# Revit family: Ebara-Grupo de presión APG VV (350-ES-600)
name_source: partatom
category: Equipos mecánicos
revit_build: Autodesk Revit 2017 (Build: 20171027_0315(x64)
units: mm (PartAtom-declared; Revit-internal decimal feet)

## family parameters
Compartido = No
Corte con vacíos al cargar = No
Cota de conector redondo = Diámetro de uso
Número OmniClass = 23.65.05.11.11
Punto de cálculo de habitación = No
Se basa en plano de trabajo = No
Siempre vertical = Sí
Tipo de pieza = Normal
Título OmniClass = Water Supply Systems

## types (1)
- Ebara-Grupo de presión APG VV (350-ES-600)
    Acabado armario = 09 96_Genérico_Esmalte blanco 255.255.255
    Acabado coloreado = 09 96_Genérico_Esmalte azul 30.137.225
    Acabado conexiones tuberías = 22 11_Genérico_Latón pulido
    Acabado estructura = 09 96_Genérico_Esmalte negro 22.22.22
    Acabado plástico gris = 06 60_Genérico_Plástico gris mate 128.128.128
    Acabado tuberías = 05 12_Genérico_Acero inoxidable AISI 304
    B00 = Ebara-Grupo de presión-Sin bomba (350-ES-600) : Sin bomba
    B01 = Ebara-Grupo de presión-Bomba EVMG (350-ES-600) : 32-2-0
    B02 = Ebara-Grupo de presión-Bomba EVMG (350-ES-600) : 32-3-1
    B03 = Ebara-Grupo de presión-Bomba EVMG (350-ES-600) : 32-4-1
    B04 = Ebara-Grupo de presión-Bomba EVMG (350-ES-600) : 32-5-3
    B05 = Ebara-Grupo de presión-Bomba EVMG (350-ES-600) : 32-5-0
    B06 = Ebara-Grupo de presión-Bomba EVMG (350-ES-600) : 32-6-2
    B07 = Ebara-Grupo de presión-Bomba EVMG (350-ES-600) : 32-7-0
    B08 = Ebara-Grupo de presión-Bomba EVMG (350-ES-600) : 45-2-2
    B09 = Ebara-Grupo de presión-Bomba EVMG (350-ES-600) : 45-2-0
    B10 = Ebara-Grupo de presión-Bomba EVMG (350-ES-600) : 45-3-0
    B11 = Ebara-Grupo de presión-Bomba EVMG (350-ES-600) : 45-4-2
    B12 = Ebara-Grupo de presión-Bomba EVMG (350-ES-600) : 45-4-0
    B13 = Ebara-Grupo de presión-Bomba EVMG (350-ES-600) : 45-5-0
    B14 = Ebara-Grupo de presión-Bomba EVMG (350-ES-600) : 64-1-0
    B15 = Ebara-Grupo de presión-Bomba EVMG (350-ES-600) : 64-2-2
    B16 = Ebara-Grupo de presión-Bomba EVMG (350-ES-600) : 64-2-0
    B17 = Ebara-Grupo de presión-Bomba EVMG (350-ES-600) : 64-3-1
    B18 = Ebara-Grupo de presión-Bomba EVMG (350-ES-600) : 64-3-2
    B19 = Ebara-Grupo de presión-Bomba EVMG (350-ES-600) : 64-4-2
    B20 = Ebara-Grupo de presión-Bomba EVMG (350-ES-600) : 64-4-3
    Bancada 32 = Ebara-Grupo de presión-Bancada APG (350-ES-600) : Serie 32
    Bancada 45 = Ebara-Grupo de presión-Bancada APG (350-ES-600) : Serie 45
    Bancada 64 = Ebara-Grupo de presión-Bancada APG (350-ES-600) : Serie 64
    C 120 = Ebara-Grupo de presión-Cuadro APG (350-ES-600) : HT 120
    C 140 = Ebara-Grupo de presión-Cuadro APG (350-ES-600) : HT 140
    C 150 = Ebara-Grupo de presión-Cuadro APG (350-ES-600) : HT 150
    C 170 = Ebara-Grupo de presión-Cuadro APG (350-ES-600) : HT 170
    Código de montaje = 50.10.10.20
    Fabricante = Ebara
    Modelo = APG VV
    URL = http://www.ebara.es
